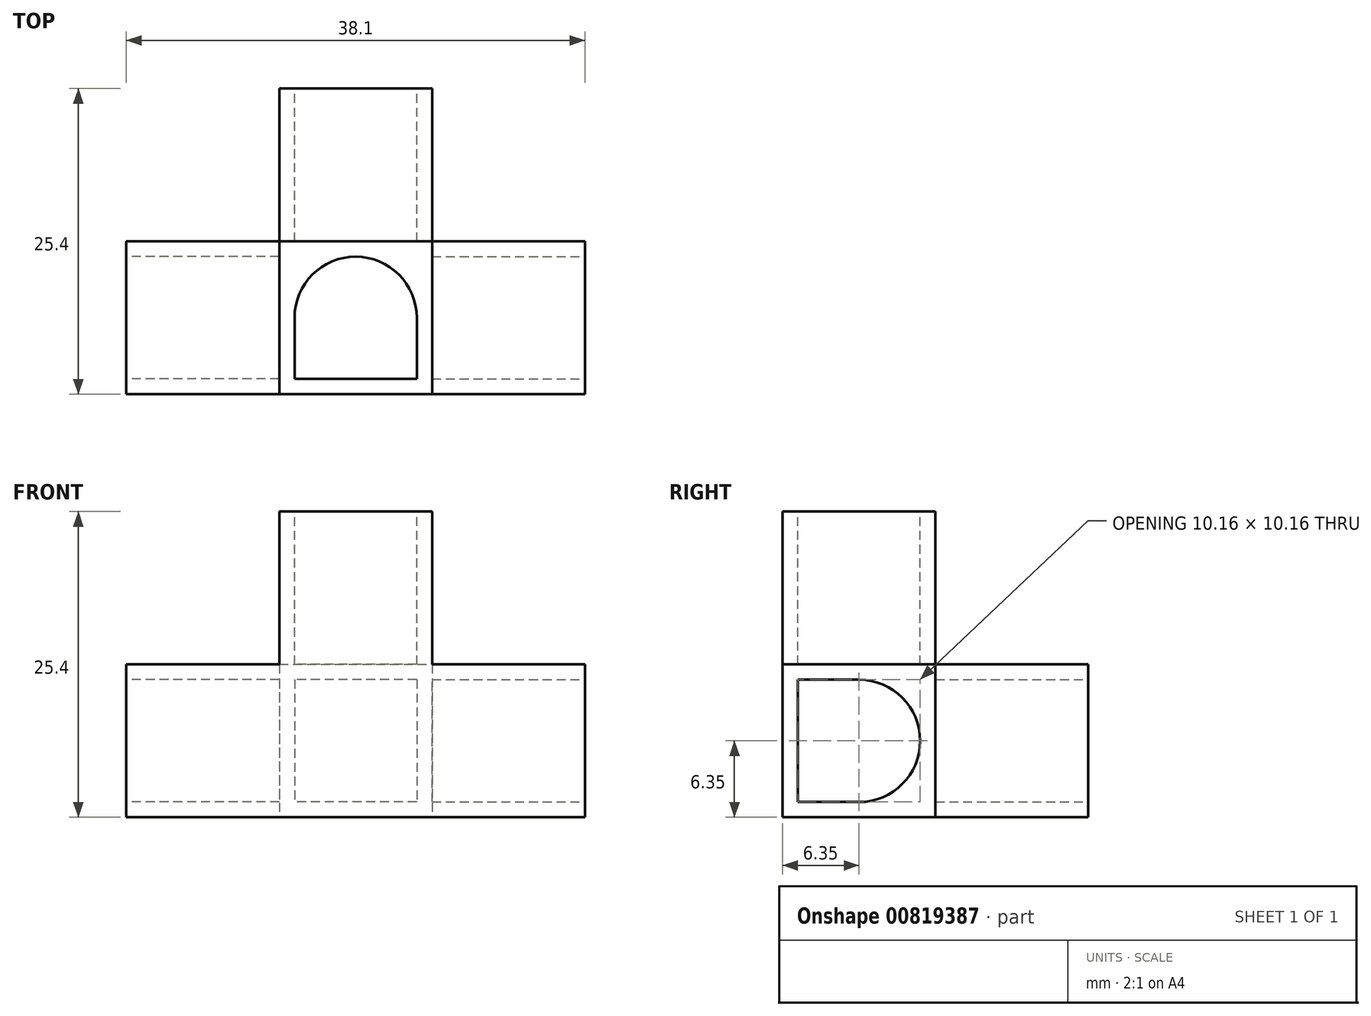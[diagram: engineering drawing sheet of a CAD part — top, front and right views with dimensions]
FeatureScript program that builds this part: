
annotation { "Feature Type Name" : "Feature", "Feature Type Description" : "" }
export const myFeature = defineFeature(function(context is Context, id is Id, definition is map)
    precondition{}
    {
        {
            var Q0;
            Q0=qCreatedBy(makeId("Top.planeOp"),FACE);
            var sketch = newSketch(context, id + "F0", { "sketchPlane" : qUnion([Q0])});
            skLineSegment(sketch, "E0", {"start": v(0, 0) * mm, "end": v(0, 12.7) * mm});
            skLineSegment(sketch, "E1", {"start": v(0, 12.7) * mm, "end": v(12.7, 12.7) * mm});
            skLineSegment(sketch, "E2", {"start": v(12.7, 12.7) * mm, "end": v(12.7, 25.4) * mm});
            skLineSegment(sketch, "E3", {"start": v(12.7, 25.4) * mm, "end": v(25.4, 25.4) * mm});
            skLineSegment(sketch, "E4", {"start": v(25.4, 25.4) * mm, "end": v(25.4, 12.7) * mm});
            skLineSegment(sketch, "E5", {"start": v(25.4, 12.7) * mm, "end": v(38.1, 12.7) * mm});
            skLineSegment(sketch, "E6", {"start": v(38.1, 12.7) * mm, "end": v(38.1, 0) * mm});
            skLineSegment(sketch, "E7", {"start": v(38.1, 0) * mm, "end": v(0, 0) * mm});
            skSolve(sketch);
        }
        {
            var Q0;
            Q0=qSketchRegion(id+"F0",true);
            extrude(context, id + "F1", {"entities" : qUnion([Q0]), "depth" : 12.7 * mm, "offsetDistance" : 25.4 * mm});
        }
        {
            var Q0;
            Q0=makeQuery(id+"F1.opExtrude","CAP_FACE",FACE,{"disambiguationData":[OSD([sQuery(id+"F0.wireOp",EDGE,"E0"),sQuery(id+"F0.wireOp",EDGE,"E1"),sQuery(id+"F0.wireOp",EDGE,"E2"),sQuery(id+"F0.wireOp",EDGE,"E3"),sQuery(id+"F0.wireOp",EDGE,"E4"),sQuery(id+"F0.wireOp",EDGE,"E5"),sQuery(id+"F0.wireOp",EDGE,"E6"),sQuery(id+"F0.wireOp",EDGE,"E7")])],"isStart":false});
            var sketch = newSketch(context, id + "F2", { "sketchPlane" : qUnion([Q0])});
            skLineSegment(sketch, "E8.bottom", {"start": v(12.7, 12.7) * mm, "end": v(25.4, 12.7) * mm});
            skLineSegment(sketch, "E8.top", {"start": v(12.7, 0) * mm, "end": v(25.4, 0) * mm});
            skLineSegment(sketch, "E8.left", {"start": v(12.7, 12.7) * mm, "end": v(12.7, 0) * mm});
            skLineSegment(sketch, "E8.right", {"start": v(25.4, 12.7) * mm, "end": v(25.4, 0) * mm});
            skSolve(sketch);
        }
        {
            var Q0;
            Q0=qSketchRegion(id+"F2",true);
            extrude(context, id + "F3", {"entities" : qUnion([Q0]), "operationType" : NewBodyOperationType.ADD, "depth" : 12.7 * mm, "offsetDistance" : 25.4 * mm});
        }
        {
            var Q0;
            Q0=makeQuery(id+"F1.opExtrude","SWEPT_FACE",FACE,{"disambiguationData":[OSD([sQuery(id+"F0.wireOp",EDGE,"E6")])]});
            var sketch = newSketch(context, id + "F4", { "sketchPlane" : qUnion([Q0])});
            skLineSegment(sketch, "E9.bottom", {"start": v(1.27, 1.27) * mm, "end": v(6.35, 1.27) * mm});
            skLineSegment(sketch, "E9.top", {"start": v(1.27, 11.43) * mm, "end": v(6.35, 11.43) * mm});
            skLineSegment(sketch, "E9.left", {"start": v(1.27, 1.27) * mm, "end": v(1.27, 11.43) * mm});
            skLineSegment(sketch, "E9.right", {"start": v(6.35, 1.27) * mm, "end": v(6.35, 11.43) * mm});
            skArc(sketch, "E10", {"start": v(6.35, 1.27) * mm, "mid": v(11.43, 6.35) * mm, "end": v(6.35, 11.43) * mm});
            skSolve(sketch);
        }
        {
            var Q0;
            Q0=makeQuery(id+"F1.opExtrude","SWEPT_FACE",FACE,{"disambiguationData":[OSD([sQuery(id+"F0.wireOp",EDGE,"E0")])]});
            var sketch = newSketch(context, id + "F5", { "sketchPlane" : qUnion([Q0])});
            skSolve(sketch);
        }
        {
            var Q0;
            Q0=qSketchRegion(id+"F4",true);
            extrude(context, id + "F6", {"entities" : qUnion([Q0]), "operationType" : NewBodyOperationType.REMOVE, "oppositeDirection" : true, "depth" : 12.7 * mm, "offsetDistance" : 25.4 * mm});
        }
        {
            var Q0;
            Q0=makeQuery(id+"F3.opExtrude","CAP_FACE",FACE,{"disambiguationData":[OSD([sQuery(id+"F2.wireOp",EDGE,"E8.bottom"),sQuery(id+"F2.wireOp",EDGE,"E8.top"),sQuery(id+"F2.wireOp",EDGE,"E8.left"),sQuery(id+"F2.wireOp",EDGE,"E8.right")])],"isStart":false});
            var sketch = newSketch(context, id + "F7", { "sketchPlane" : qUnion([Q0])});
            skLineSegment(sketch, "E11.bottom", {"start": v(24.13, 1.27) * mm, "end": v(13.97, 1.27) * mm});
            skLineSegment(sketch, "E11.top", {"start": v(24.13, 6.35) * mm, "end": v(13.97, 6.35) * mm});
            skLineSegment(sketch, "E11.left", {"start": v(24.13, 1.27) * mm, "end": v(24.13, 6.35) * mm});
            skLineSegment(sketch, "E11.right", {"start": v(13.97, 1.27) * mm, "end": v(13.97, 6.35) * mm});
            skArc(sketch, "E12", {"start": v(24.13, 6.35) * mm, "mid": v(19.05, 11.43) * mm, "end": v(13.97, 6.35) * mm});
            skSolve(sketch);
        }
        {
            var Q0;
            Q0=qSketchRegion(id+"F7",true);
            extrude(context, id + "F8", {"entities" : qUnion([Q0]), "operationType" : NewBodyOperationType.REMOVE, "oppositeDirection" : true, "depth" : 12.7 * mm, "offsetDistance" : 25.4 * mm});
        }
        {
            var Q0;
            {var subQ0=sQuery(id+"F0.wireOp",EDGE,"E0");Q0=makeQuery(id+"F5.imprint","IMPRINT",FACE,{"disambiguationData":[TD([[makeQuery(id+"F5.imprint","IMPRINT",EDGE,{"derivedFrom":makeQuery(id+"F1.opExtrude","CAP_EDGE",EDGE,{"disambiguationData":[OSD([subQ0])],"isStart":true})}),-1.0]])]});}
            var sketch = newSketch(context, id + "F9", { "sketchPlane" : qUnion([Q0])});
            skLineSegment(sketch, "E13.bottom", {"start": v(-1.27, 11.43) * mm, "end": v(-6.35, 11.43) * mm});
            skLineSegment(sketch, "E13.top", {"start": v(-1.27, 1.27) * mm, "end": v(-6.35, 1.27) * mm});
            skLineSegment(sketch, "E13.left", {"start": v(-1.27, 11.43) * mm, "end": v(-1.27, 1.27) * mm});
            skLineSegment(sketch, "E13.right", {"start": v(-6.35, 11.43) * mm, "end": v(-6.35, 1.27) * mm});
            skArc(sketch, "E14", {"start": v(-6.35, 11.43) * mm, "mid": v(-11.43, 6.35) * mm, "end": v(-6.35, 1.27) * mm});
            skSolve(sketch);
        }
        {
            var Q0;
            Q0=qSketchRegion(id+"F9",true);
            extrude(context, id + "F10", {"entities" : qUnion([Q0]), "operationType" : NewBodyOperationType.REMOVE, "oppositeDirection" : true, "depth" : 12.7 * mm, "offsetDistance" : 25.4 * mm});
        }
        {
            var Q0;
            Q0=makeQuery(id+"F1.opExtrude","SWEPT_FACE",FACE,{"disambiguationData":[OSD([sQuery(id+"F0.wireOp",EDGE,"E3")])]});
            var sketch = newSketch(context, id + "F11", { "sketchPlane" : qUnion([Q0])});
            skLineSegment(sketch, "E15.bottom", {"start": v(-24.13, 11.43) * mm, "end": v(-13.97, 11.43) * mm});
            skLineSegment(sketch, "E15.top", {"start": v(-24.13, 1.27) * mm, "end": v(-13.97, 1.27) * mm});
            skLineSegment(sketch, "E15.left", {"start": v(-24.13, 11.43) * mm, "end": v(-24.13, 1.27) * mm});
            skLineSegment(sketch, "E15.right", {"start": v(-13.97, 11.43) * mm, "end": v(-13.97, 1.27) * mm});
            skSolve(sketch);
        }
        {
            var Q0;
            Q0=qSketchRegion(id+"F11",true);
            extrude(context, id + "F12", {"entities" : qUnion([Q0]), "operationType" : NewBodyOperationType.REMOVE, "oppositeDirection" : true, "depth" : 12.7 * mm, "offsetDistance" : 25.4 * mm});
        }
    });
